# Revit family: QF_Vollrath_FC-HCF-01120-AD
name_source: partatom
category: Specialty Equipment
units: mm (PartAtom-declared; Revit-internal decimal feet)

## family parameters
Always vertical = Yes
Cut with Voids When Loaded = Yes
OmniClass Number = 23.40.40.00
OmniClass Title = Food Service Equipment and Furnishings
Part Type = Normal
Room Calculation Point = No
Round Connector Dimension = Use Diameter
Shared = No
Work Plane-Based = Yes

## types (1)
- 120 Volt
    Apparent Power = 612 VA
    Assembly Code = E1090320
    CSI MasterFormat = 11 46 16
    Conn Conduit = Yes
    Conn Plug = NEMA 5-15P
    Cutout Depth = 25.25 "
    Cutout Width = 17.325 "
    Cycle = 60 Hz
    Default Elevation = 0 "
    Depth = 26 "
    Description = Drop In, Hot/Cold
    Electric Connection Type = -
    FL Amps = 5 A
    Foodservice Equipment Identifier = Yes
    HP = .25
    Indirect Waste Connection Height = 0 "
    Indirect Waste Size = 1"
    Indirect Waste Size OD = 1"
    KCL SpecSheet URL = http://kcl5.kclcad.com
    Manufacturer = Vollrath
    Model = FC-6HC-01120-AD
    Phase = 1
    URL = www.vollrath.com
    Volts = 120 V
    Watts = 625 W
    Weight in Pounds = 107
    Width = 18.033 "

## geometry (parser evidence)
native form markers: Sweep x2
no freeform markers — native parametric forms only
